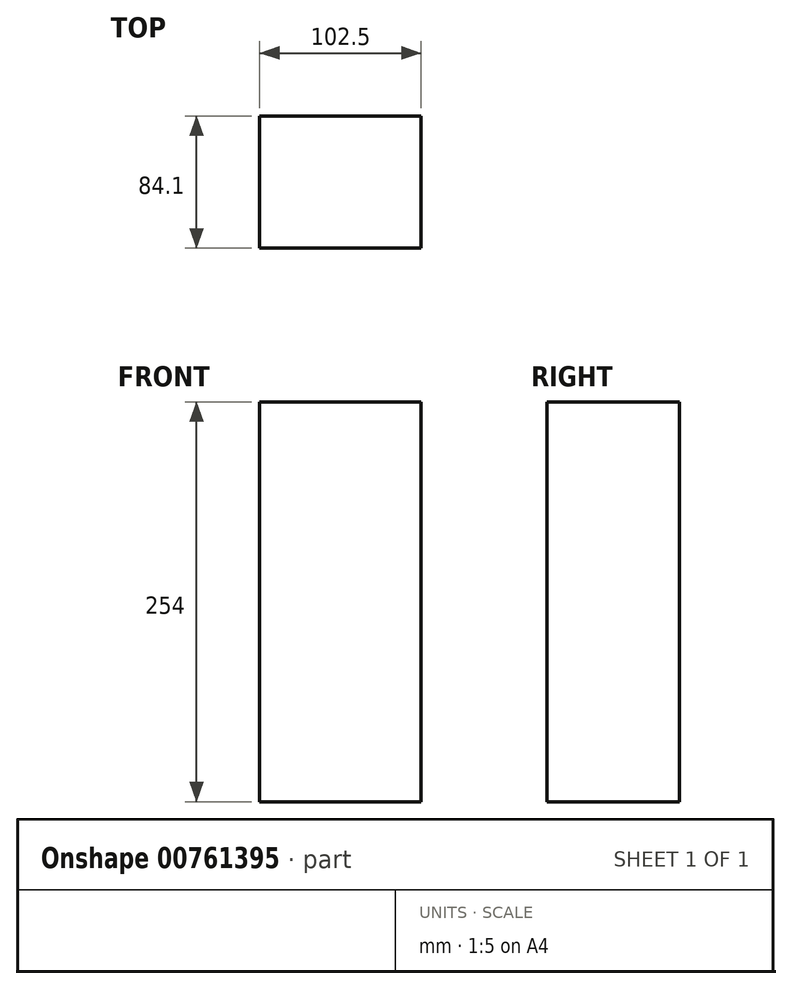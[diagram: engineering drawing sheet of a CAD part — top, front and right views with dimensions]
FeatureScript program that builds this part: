
annotation { "Feature Type Name" : "Feature", "Feature Type Description" : "" }
export const myFeature = defineFeature(function(context is Context, id is Id, definition is map)
    precondition{}
    {
        {
            var Q0;
            Q0=qCreatedBy(makeId("Top.planeOp"),FACE);
            var sketch = newSketch(context, id + "F0", { "sketchPlane" : qUnion([Q0])});
            skLineSegment(sketch, "E0", {"start": v(-52.7, 53.3) * mm, "end": v(49.79, 53.3) * mm});
            skLineSegment(sketch, "E1", {"start": v(49.79, 53.3) * mm, "end": v(49.79, -30.8) * mm});
            skLineSegment(sketch, "E2", {"start": v(49.79, -30.8) * mm, "end": v(-52.7, -30.8) * mm});
            skLineSegment(sketch, "E3", {"start": v(-52.7, -30.8) * mm, "end": v(-52.7, 53.3) * mm});
            skSolve(sketch);
        }
        {
            var Q0;
            Q0=makeQuery(id+"F0.imprint","IMPRINT",FACE,{"disambiguationData":[TD([[makeQuery(id+"F0.imprint","IMPRINT",EDGE,{"derivedFrom":sQuery(id+"F0.wireOp",EDGE,"E0")}),-1.0]])]});
            extrude(context, id + "F1", {"entities" : qUnion([Q0]), "depth" : 254 * mm, "offsetDistance" : 25.4 * mm});
        }
    });
